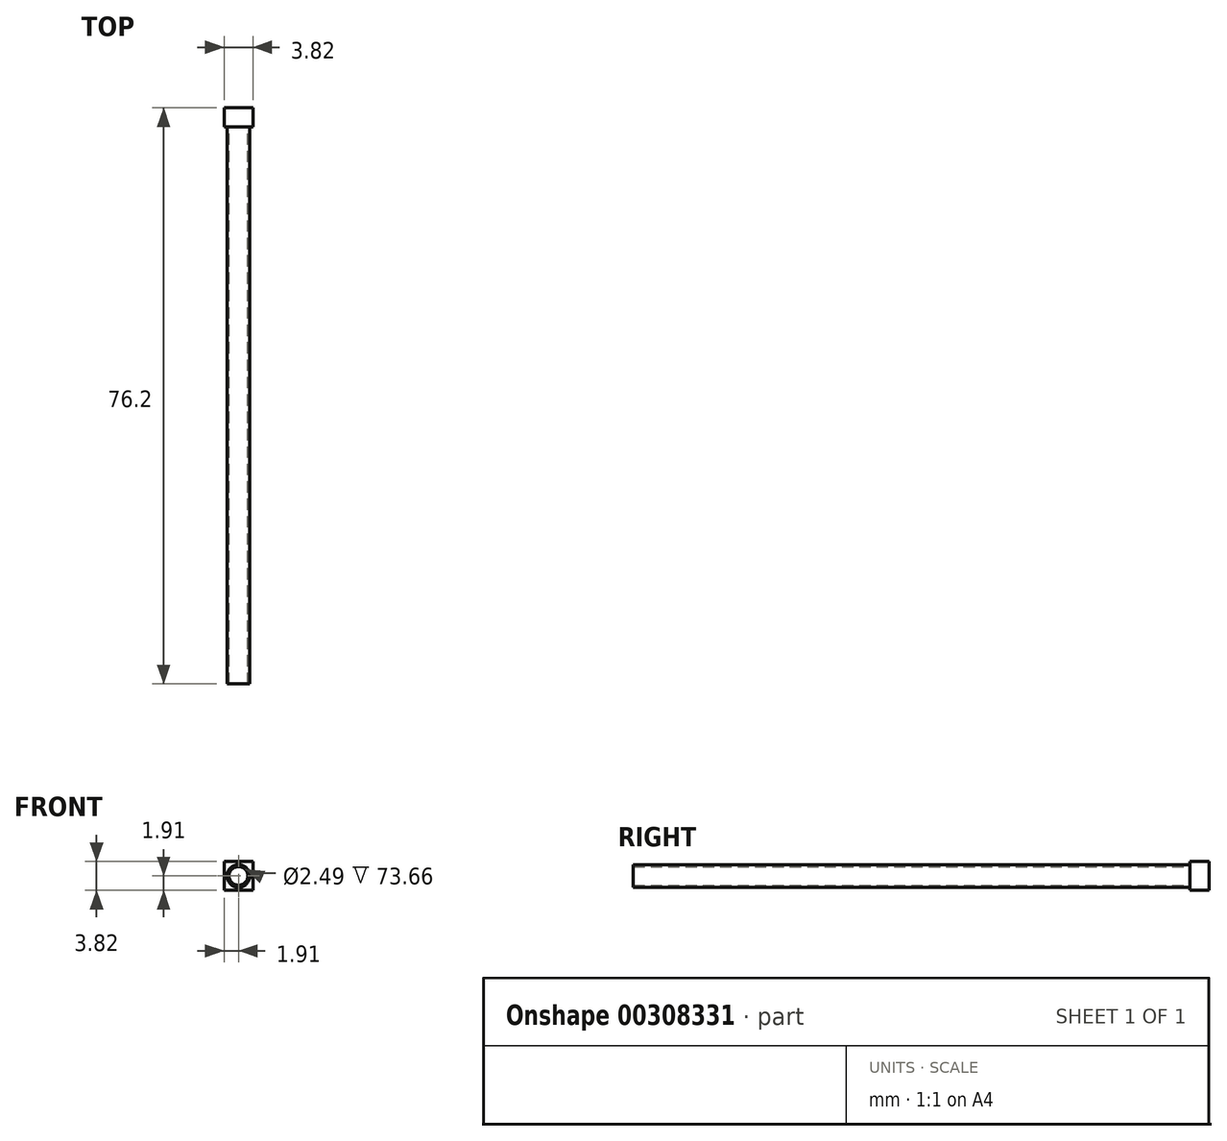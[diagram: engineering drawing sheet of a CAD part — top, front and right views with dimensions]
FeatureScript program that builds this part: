
annotation { "Feature Type Name" : "Feature", "Feature Type Description" : "" }
export const myFeature = defineFeature(function(context is Context, id is Id, definition is map)
    precondition{}
    {
        {
            var Q0;
            Q0=qCreatedBy(makeId("Front.planeOp"),FACE);
            var sketch = newSketch(context, id + "F0", { "sketchPlane" : qUnion([Q0])});
            skCircle(sketch, "E0", {"center": v(0, 0) * mm, "radius": 1.5 * mm});
            skCircle(sketch, "E1", {"center": v(0, 0) * mm, "radius": 1.25 * mm});
            skLineSegment(sketch, "E2.bottom", {"start": v(-1.9, 1.9) * mm, "end": v(1.9, 1.9) * mm});
            skLineSegment(sketch, "E2.top", {"start": v(-1.9, -1.9) * mm, "end": v(1.9, -1.9) * mm});
            skLineSegment(sketch, "E2.left", {"start": v(-1.9, 1.9) * mm, "end": v(-1.9, -1.9) * mm});
            skLineSegment(sketch, "E2.right", {"start": v(1.9, 1.9) * mm, "end": v(1.9, -1.9) * mm});
            skSolve(sketch);
        }
        {
            var Q0;
            Q0=makeQuery(id+"F0.imprint","IMPRINT",FACE,{"disambiguationData":[TD([[makeQuery(id+"F0.imprint","IMPRINT",EDGE,{"derivedFrom":sQuery(id+"F0.wireOp",EDGE,"E0")}),1.0]])]});
            extrude(context, id + "F1", {"entities" : qUnion([Q0]), "depth" : 76.2 * mm});
        }
        {
            var Q0;
            Q0=makeQuery(id+"F0.imprint","IMPRINT",FACE,{"disambiguationData":[TD([[makeQuery(id+"F0.imprint","IMPRINT",EDGE,{"derivedFrom":sQuery(id+"F0.wireOp",EDGE,"E1")}),1.0]])]});
            var Q1;
            Q1=makeQuery(id+"F0.imprint","IMPRINT",FACE,{"disambiguationData":[TD([[makeQuery(id+"F0.imprint","IMPRINT",EDGE,{"derivedFrom":sQuery(id+"F0.wireOp",EDGE,"E0")}),-1.0]])]});
            extrude(context, id + "F2", {"entities" : qUnion([Q0, Q1]), "operationType" : NewBodyOperationType.ADD, "depth" : 2.54 * mm});
        }
    });
